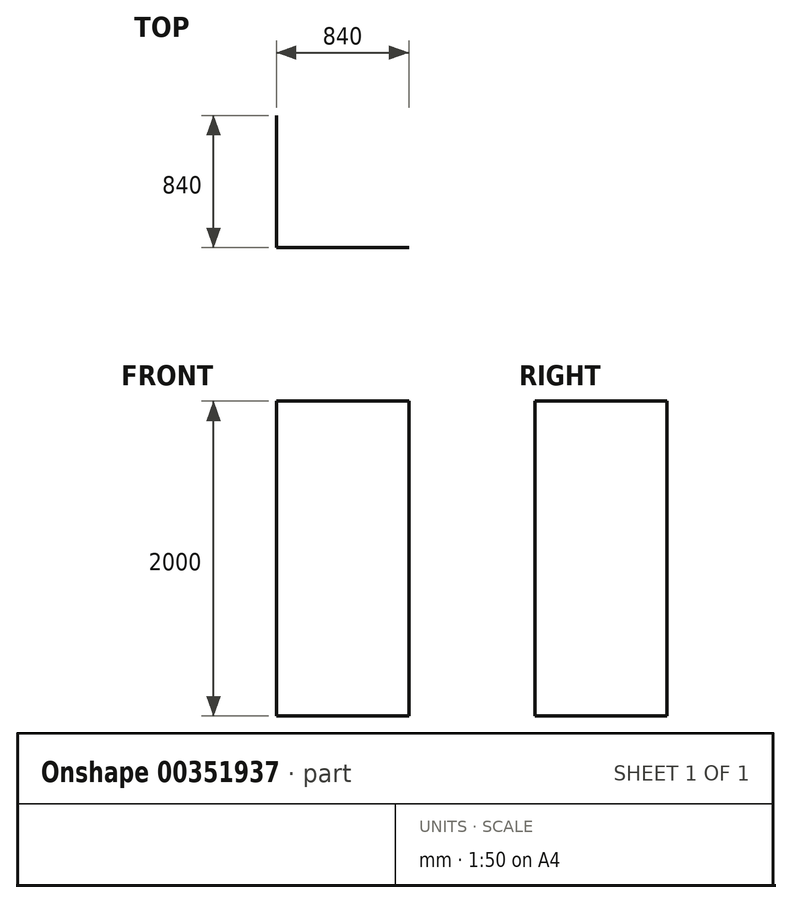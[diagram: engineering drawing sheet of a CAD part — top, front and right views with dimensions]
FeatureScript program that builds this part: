
annotation { "Feature Type Name" : "Feature", "Feature Type Description" : "" }
export const myFeature = defineFeature(function(context is Context, id is Id, definition is map)
    precondition{}
    {
        {
            var Q0;
            Q0=qCreatedBy(makeId("Top.planeOp"),FACE);
            var sketch = newSketch(context, id + "F0", { "sketchPlane" : qUnion([Q0])});
            skLineSegment(sketch, "E0", {"start": v(-46.41, 13.32) * mm, "end": v(793.59, 13.32) * mm});
            skLineSegment(sketch, "E1", {"start": v(-46.41, 13.32) * mm, "end": v(-46.41, 853.32) * mm});
            skArc(sketch, "E2", {"start": v(793.59, 13.32) * mm, "mid": v(547.56, 607.28) * mm, "end": v(-46.41, 853.32) * mm});
            skSolve(sketch);
        }
        {
            var Q0;
            Q0 = qSketchRegion(id + "F0", true);
            var Q1;
            Q1=sQuery(id+"F0.wireOp",EDGE,"E1");
            var Q2;
            Q2=sQuery(id+"F0.wireOp",EDGE,"E0");
            extrude(context, id + "F1", {"entities" : qUnion([Q0]), "bodyType" : ToolBodyType.SURFACE, "surfaceEntities" : qUnion([Q1, Q2]), "depth" : 2000 * mm});
        }
    });
